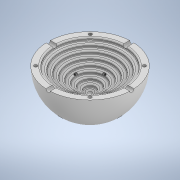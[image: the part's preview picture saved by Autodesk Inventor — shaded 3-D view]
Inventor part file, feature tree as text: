
AUTODESK INVENTOR PART (.ipt)
format: ipt  version: 2022 (Build 260153000, 153)  size: 520,704 bytes
history: native  units: mm
features: extrude x16, sketch x16, other x9, fillet x5
ambient origin geometry x8: Origin, YZ Plane, XZ Plane, XY Plane, X Axis, Y Axis, Z Axis, Center Point
bodies: Body1 (feature_tree)
feature tree (46):
  other  "實體1"
  extrude  "擠出1"  Depth=60.0mm
  fillet  "圓角1"  Radius=30.0mm
  extrude  "擠出2"  Depth=30.0mm
  extrude  "擠出3"  Depth=50.0mm
  extrude  "擠出4"  Depth=2.0mm TaperAngle=0.0deg
  extrude  "擠出5"  Depth=44.0mm
  extrude  "擠出6"  Depth=2.0mm TaperAngle=0.0deg
  extrude  "擠出7"  Depth=38.0mm
  extrude  "擠出8"  Depth=2.0mm TaperAngle=0.0deg
  extrude  "擠出9"  Depth=32.0mm
  extrude  "擠出11"  Depth=2.0mm TaperAngle=0.0deg
  extrude  "擠出12"  Depth=26.0mm
  extrude  "擠出13"  Depth=2.0mm TaperAngle=0.0deg
  extrude  "擠出16"  Depth=20.0mm
  fillet  "圓角2"  Radius=2.0mm
  extrude  "擠出17"  Depth=14.0mm
  fillet  "圓角3"  Radius=2.0mm
  extrude  "擠出18"  Depth=8.0mm
  fillet  "圓角4"  Radius=2.0mm
  extrude  "擠出19"  Depth=3.0mm
  fillet  "圓角5"  Radius=20.0mm
  other  "面圓角1"
  other  "面圓角2"
  other  "面圓角3"
  other  "面圓角4"
  other  "面圓角5"
  other  "面圓角6"
  other  "面圓角7"
  other  "面圓角8"
  sketch  "草圖3"
  sketch  "草圖4"
  sketch  "草圖5"
  sketch  "草圖6"
  sketch  "草圖7"
  sketch  "草圖8"
  sketch  "草圖9"
  sketch  "草圖10"
  sketch  "草圖11"
  sketch  "草圖14"
  sketch  "草圖15"
  sketch  "草圖16"
  sketch  "草圖25"
  sketch  "草圖26"
  sketch  "草圖27"
  sketch  "草圖29"
